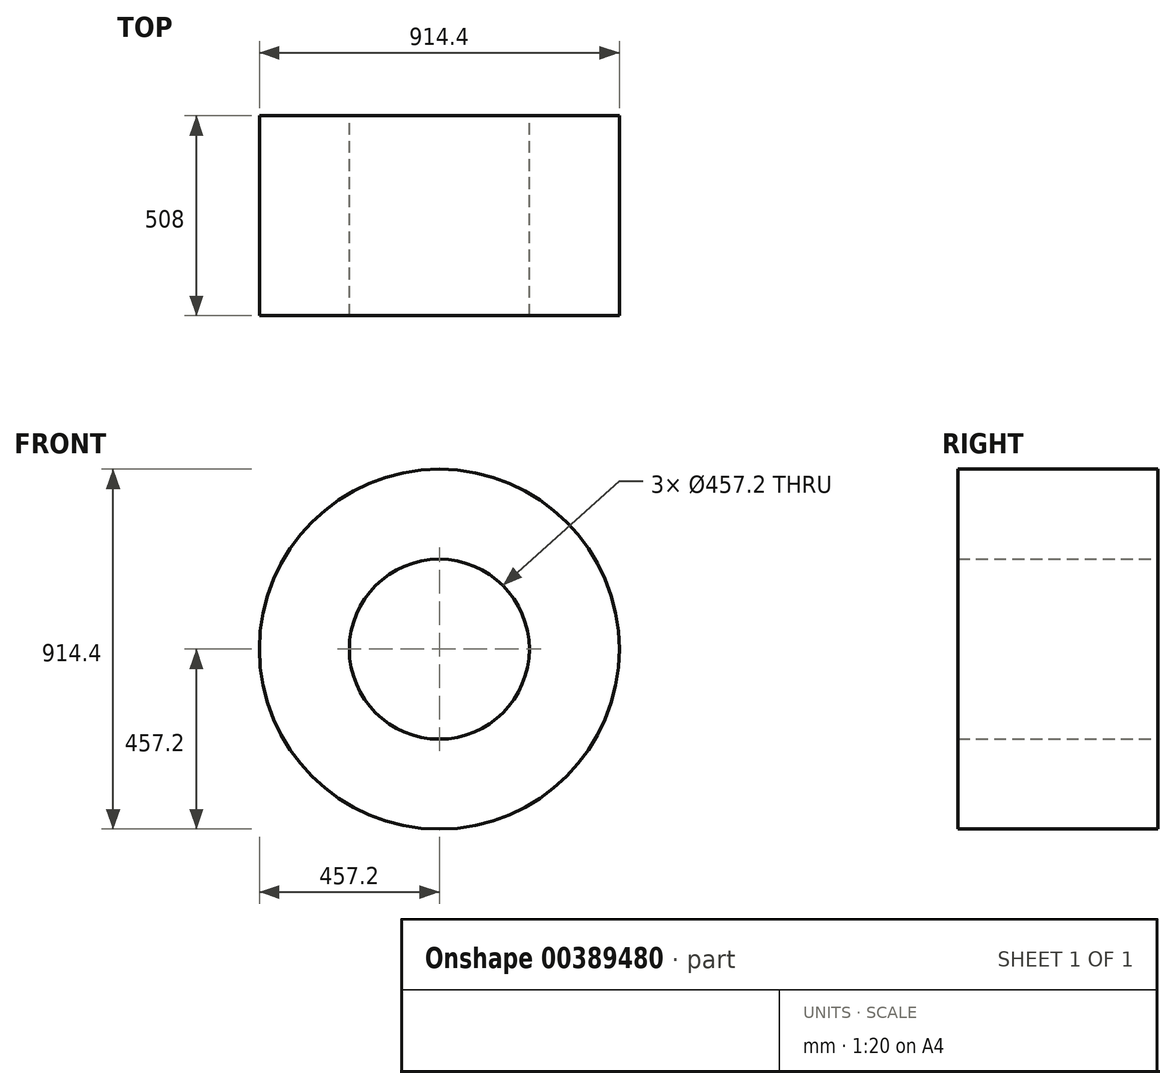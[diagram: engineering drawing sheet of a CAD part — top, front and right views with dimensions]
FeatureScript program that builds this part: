
annotation { "Feature Type Name" : "Feature", "Feature Type Description" : "" }
export const myFeature = defineFeature(function(context is Context, id is Id, definition is map)
    precondition{}
    {
        {
            var Q0;
            Q0=qCreatedBy(makeId("Front.planeOp"),FACE);
            var sketch = newSketch(context, id + "F0", { "sketchPlane" : qUnion([Q0])});
            skCircle(sketch, "E0", {"center": v(0, 0) * mm, "radius": 457.2 * mm});
            skCircle(sketch, "E1", {"center": v(0, 0) * mm, "radius": 228.6 * mm});
            skSolve(sketch);
        }
        {
            var Q0;
            Q0 = qSketchRegion(id + "F0", true);
            extrude(context, id + "F1", {"entities" : qUnion([Q0]), "depth" : 508 * mm});
        }
    });
